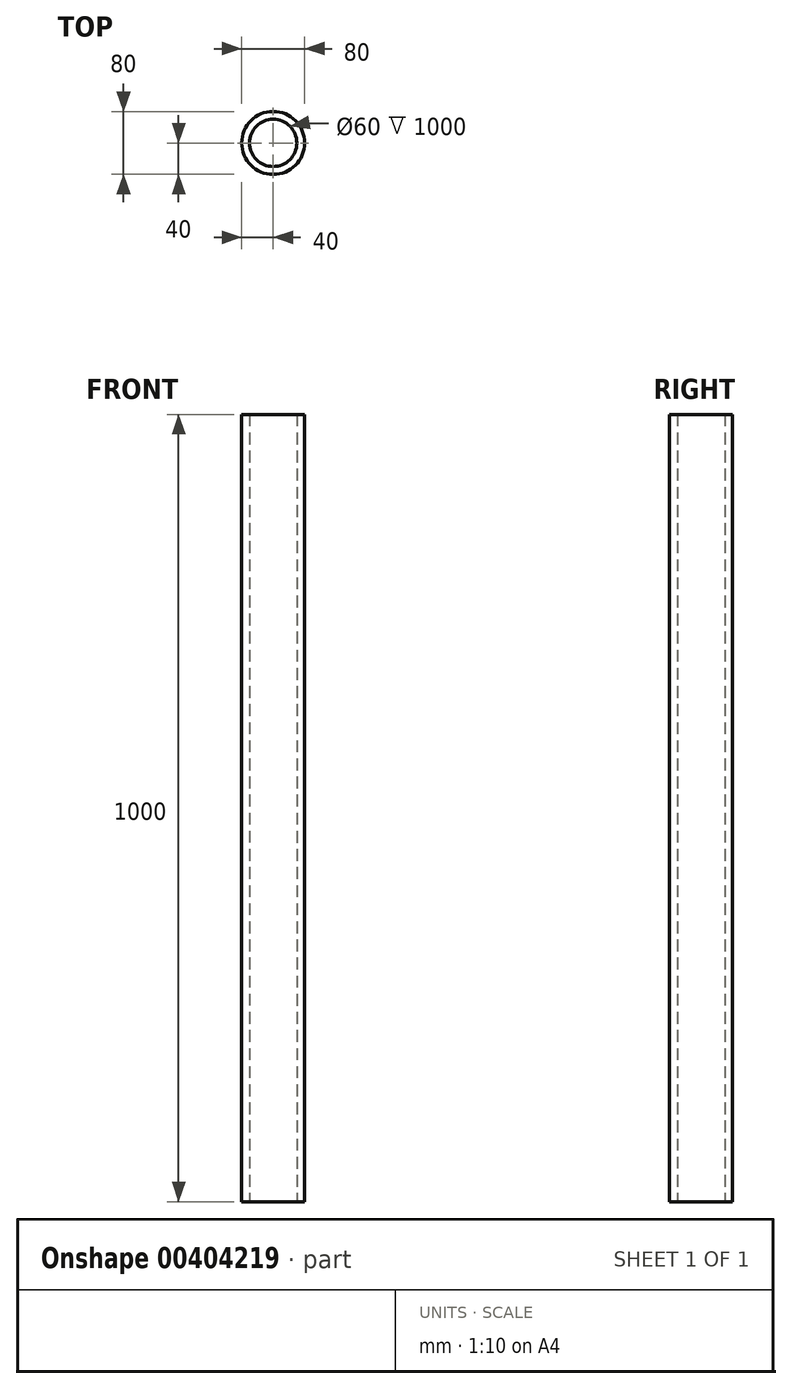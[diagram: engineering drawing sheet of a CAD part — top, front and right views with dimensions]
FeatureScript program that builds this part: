
annotation { "Feature Type Name" : "Feature", "Feature Type Description" : "" }
export const myFeature = defineFeature(function(context is Context, id is Id, definition is map)
    precondition{}
    {
        {
            var Q0;
            Q0=qCreatedBy(makeId("Top.planeOp"),FACE);
            var sketch = newSketch(context, id + "F0", { "sketchPlane" : qUnion([Q0])});
            skCircle(sketch, "E0", {"center": v(0, 0) * mm, "radius": 30 * mm});
            skCircle(sketch, "E1", {"center": v(0, 0) * mm, "radius": 40 * mm});
            skSolve(sketch);
        }
        {
            var Q0;
            Q0=makeQuery(id+"F0.imprint","IMPRINT",FACE,{"disambiguationData":[TD([[makeQuery(id+"F0.imprint","IMPRINT",EDGE,{"derivedFrom":sQuery(id+"F0.wireOp",EDGE,"E0")}),-1.0]])]});
            extrude(context, id + "F1", {"entities" : qUnion([Q0]), "depth" : 1000 * mm});
        }
    });
